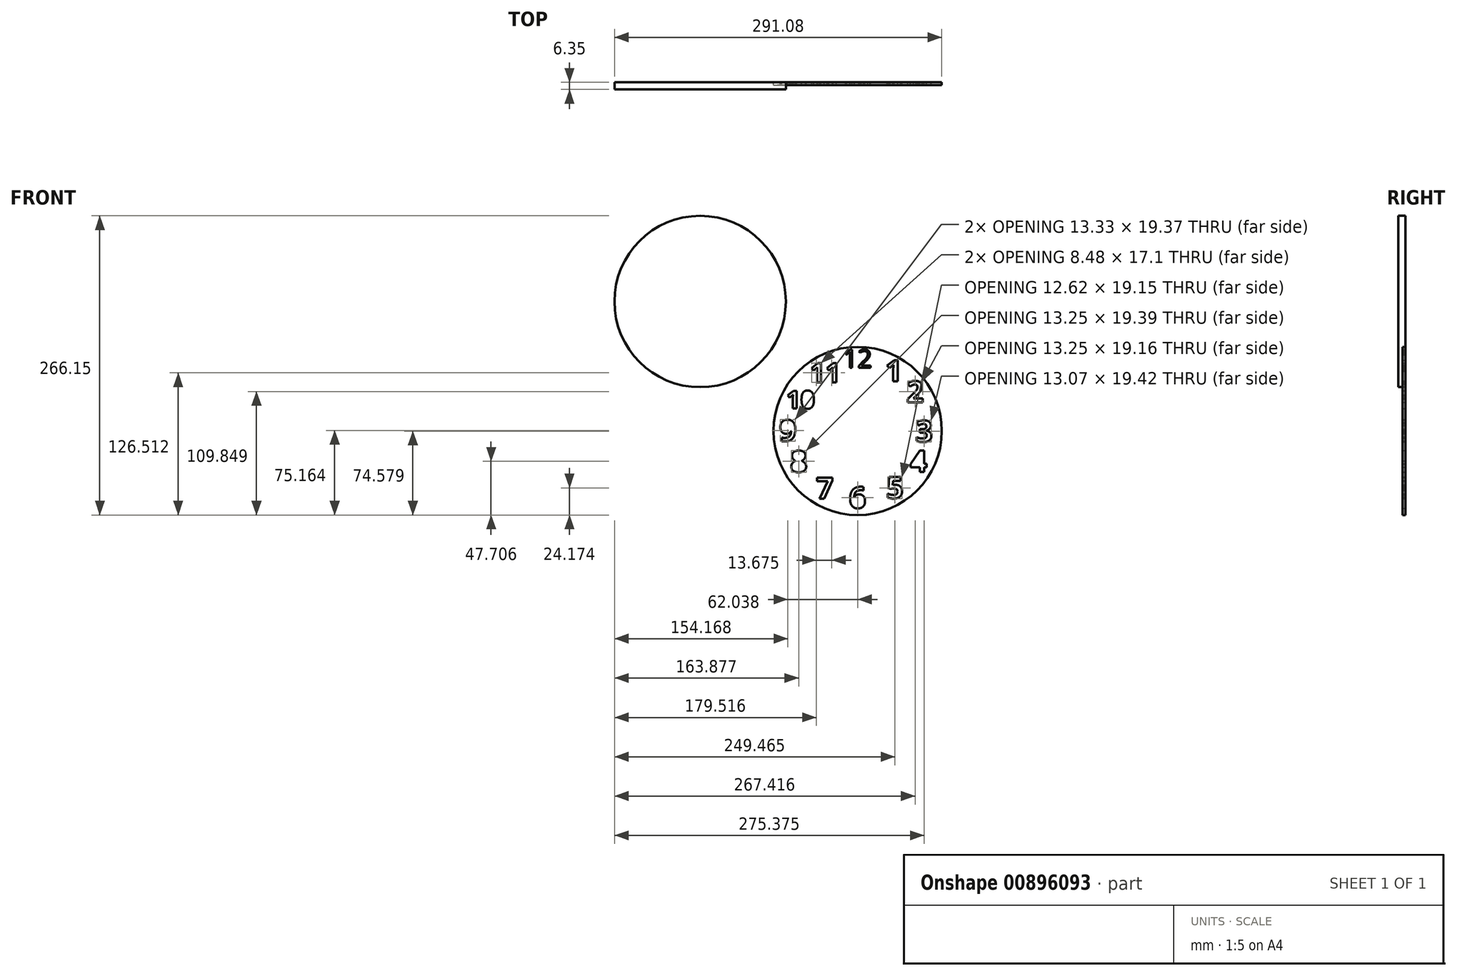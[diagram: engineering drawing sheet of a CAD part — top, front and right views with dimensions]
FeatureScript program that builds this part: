
annotation { "Feature Type Name" : "Feature", "Feature Type Description" : "" }
export const myFeature = defineFeature(function(context is Context, id is Id, definition is map)
    precondition{}
    {
        {
            var Q0;
            Q0=qCreatedBy(makeId("Front.planeOp"),FACE);
            var sketch = newSketch(context, id + "F0", { "sketchPlane" : qUnion([Q0])});
            skCircle(sketch, "E0", {"center": v(0, 0) * mm, "radius": 74.8 * mm});
            skText(sketch, "E1", { "text": "12", "fontName": "OpenSans-Regular.ttf"});
            skText(sketch, "E2", { "text": "3", "fontName": "OpenSans-Bold.ttf"});
            skText(sketch, "E3", { "text": "6", "fontName": "OpenSans-Bold.ttf"});
            skText(sketch, "E4", { "text": "9", "fontName": "OpenSans-Bold.ttf"});
            skText(sketch, "E5", { "text": "1", "fontName": "OpenSans-Bold.ttf"});
            skText(sketch, "E6", { "text": "2", "fontName": "OpenSans-Bold.ttf"});
            skText(sketch, "E7", { "text": "4", "fontName": "OpenSans-Bold.ttf"});
            skText(sketch, "E8", { "text": "5", "fontName": "OpenSans-Bold.ttf"});
            skText(sketch, "E9", { "text": "7", "fontName": "OpenSans-Bold.ttf"});
            skText(sketch, "E10", { "text": "8", "fontName": "OpenSans-Bold.ttf"});
            skText(sketch, "E11", { "text": "10", "fontName": "OpenSans-Bold.ttf"});
            skText(sketch, "E12", { "text": "11", "fontName": "OpenSans-Bold.ttf"});
            skLineSegment(sketch, "E13", {"start": v(0, 0) * mm, "end": v(0, 0) * mm});
            const initialGuessF0  = {"E1": [-0.01293, 0.05635, 1, 0, 0.01613], "E2": [0.05155, -0.00967, 1, 0, 0.01905], "E3": [-0.00767, -0.0687, 1, 0, 0.01905], "E4": [-0.06963, -0.00906, 1, 0, 0.01905], "E5": [0.0247, 0.04416, 1, 0, 0.01905], "E6": [0.0435, 0.02547, 1, 0, 0.01905], "E7": [0.04668, -0.03632, 1, 0, 0.01905], "E8": [0.02558, -0.05994, 1, 0, 0.01905], "E9": [-0.03674, -0.06032, 1, 0, 0.01905], "E10": [-0.05996, -0.03653, 1, 0, 0.01905], "E11": [-0.06342, 0.01992, 1, 0, 0.01597], "E12": [-0.04242, 0.04316, 1, 0, 0.01725]};
            skSetInitialGuess(sketch, initialGuessF0);
            skSolve(sketch);
        }
        {
            var Q0;
            Q0 = qSketchRegion(id + "F0", true);
            extrude(context, id + "F1", {"entities" : qUnion([Q0]), "depth" : 2.54 * mm, "offsetDistance" : 25.4 * mm});
        }
        {
            var Q0;
            Q0=qCreatedBy(makeId("Front.planeOp"),FACE);
            var sketch = newSketch(context, id + "F2", { "sketchPlane" : qUnion([Q0])});
            skCircle(sketch, "E14", {"center": v(-140.08, 115.15) * mm, "radius": 76.2 * mm});
            skSolve(sketch);
        }
        {
            var Q0;
            Q0 = qSketchRegion(id + "F2", true);
            extrude(context, id + "F3", {"entities" : qUnion([Q0]), "depth" : 6.35 * mm, "offsetDistance" : 25.4 * mm});
        }
    });
